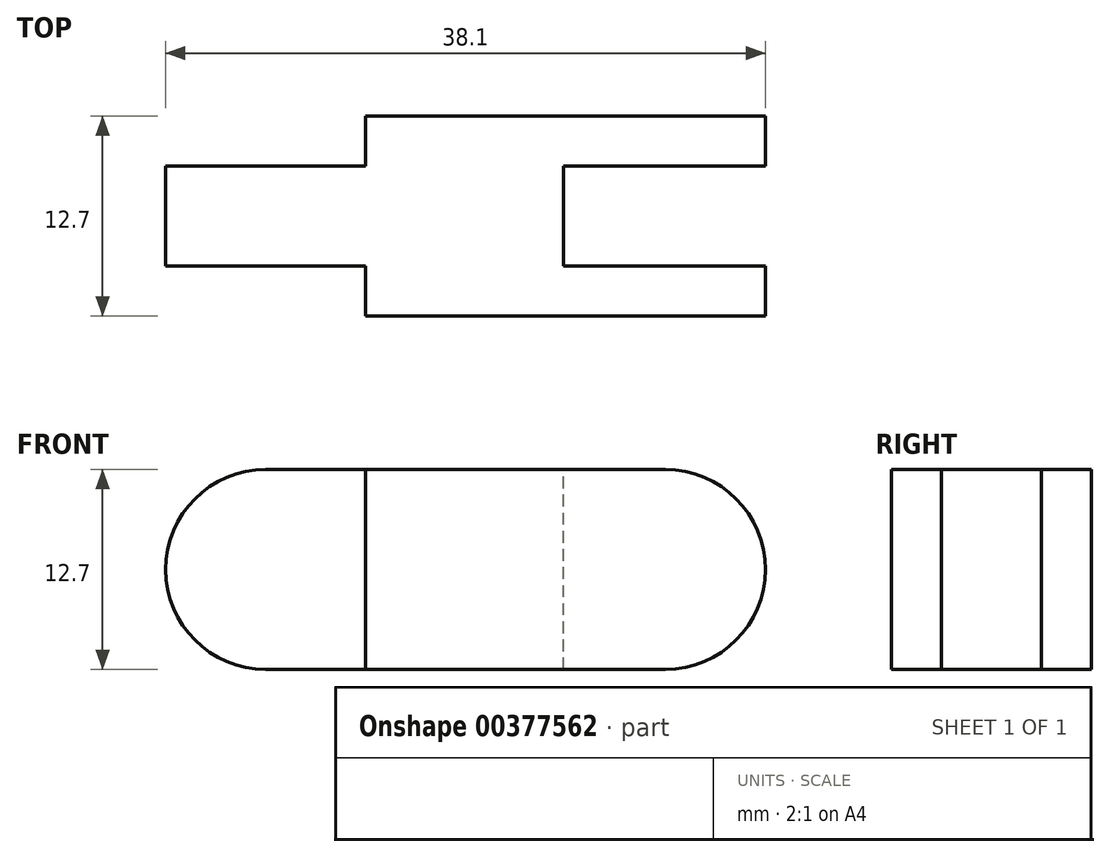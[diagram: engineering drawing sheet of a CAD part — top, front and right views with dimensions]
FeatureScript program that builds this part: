
annotation { "Feature Type Name" : "Feature", "Feature Type Description" : "" }
export const myFeature = defineFeature(function(context is Context, id is Id, definition is map)
    precondition{}
    {
        {
            var Q0;
            Q0=qCreatedBy(makeId("Front.planeOp"),FACE);
            var sketch = newSketch(context, id + "F0", { "sketchPlane" : qUnion([Q0])});
            skLineSegment(sketch, "E0.bottom", {"start": v(6.35, 0) * mm, "end": v(38.1, 0) * mm});
            skLineSegment(sketch, "E0.top", {"start": v(6.35, 12.7) * mm, "end": v(38.1, 12.7) * mm});
            skLineSegment(sketch, "E0.left", {"start": v(0, 6.35) * mm, "end": v(0, 6.35) * mm});
            skLineSegment(sketch, "E0.right", {"start": v(38.1, 0) * mm, "end": v(38.1, 12.7) * mm});
            skPoint(sketch, "E1.visualSharp", {"position": v(0, 12.7) * mm});
            skArc(sketch, "E1.filletArc", {"start": v(6.35, 12.7) * mm, "mid": v(1.86, 10.84) * mm, "end": v(0, 6.35) * mm});
            skPoint(sketch, "E2.visualSharp", {"position": v(0, 0) * mm});
            skArc(sketch, "E2.filletArc", {"start": v(0, 6.35) * mm, "mid": v(1.86, 1.86) * mm, "end": v(6.35, 0) * mm});
            skSolve(sketch);
        }
        {
            var Q0;
            Q0=qSketchRegion(id+"F0",true);
            extrude(context, id + "F1", {"entities" : qUnion([Q0]), "depth" : 3.17 * mm});
        }
        {
            var Q0;
            Q0=makeQuery(id+"F1.opExtrude","CAP_FACE",FACE,{"disambiguationData":[OSD([sQuery(id+"F0.wireOp",EDGE,"E0.bottom"),sQuery(id+"F0.wireOp",EDGE,"E0.top"),sQuery(id+"F0.wireOp",EDGE,"E0.right"),sQuery(id+"F0.wireOp",EDGE,"E1.filletArc"),sQuery(id+"F0.wireOp",EDGE,"E2.filletArc")])],"isStart":false});
            var sketch = newSketch(context, id + "F2", { "sketchPlane" : qUnion([Q0])});
            skLineSegment(sketch, "E3.bottom", {"start": v(38.1, 12.7) * mm, "end": v(12.7, 12.7) * mm});
            skLineSegment(sketch, "E3.top", {"start": v(38.1, 0) * mm, "end": v(12.7, 0) * mm});
            skLineSegment(sketch, "E3.left", {"start": v(38.1, 12.7) * mm, "end": v(38.1, 0) * mm});
            skLineSegment(sketch, "E3.right", {"start": v(12.7, 12.7) * mm, "end": v(12.7, 0) * mm});
            skSolve(sketch);
        }
        {
            var Q0;
            Q0=qSketchRegion(id+"F2",true);
            extrude(context, id + "F3", {"entities" : qUnion([Q0]), "operationType" : NewBodyOperationType.ADD, "depth" : 3.17 * mm});
        }
        {
            var Q0;
            Q0=makeQuery(id+"F3.boolean.opBoolean","MERGE",EDGE,{"derivedFrom":[makeQuery(id+"F1.opExtrude","SWEPT_EDGE",EDGE,{"disambiguationData":[OSD([sQuery(id+"F0.wireOp",EDGE,"E0.top"),sQuery(id+"F0.wireOp",EDGE,"E0.right")])]}),makeQuery(id+"F3.opExtrude","SWEPT_EDGE",EDGE,{"disambiguationData":[OSD([sQuery(id+"F2.wireOp",EDGE,"E3.bottom"),sQuery(id+"F2.wireOp",EDGE,"E3.left")])]})]});
            var Q1;
            Q1=makeQuery(id+"F3.boolean.opBoolean","MERGE",EDGE,{"derivedFrom":[makeQuery(id+"F1.opExtrude","SWEPT_EDGE",EDGE,{"disambiguationData":[OSD([sQuery(id+"F0.wireOp",EDGE,"E0.bottom"),sQuery(id+"F0.wireOp",EDGE,"E0.right")])]}),makeQuery(id+"F3.opExtrude","SWEPT_EDGE",EDGE,{"disambiguationData":[OSD([sQuery(id+"F2.wireOp",EDGE,"E3.top"),sQuery(id+"F2.wireOp",EDGE,"E3.left")])]})]});
            fillet(context, id + "F4", {"entities" : qUnion([Q0, Q1]), "radius" : 6.35 * mm, "tangentPropagation" : true, "allowEdgeOverflow" : false});
        }
        {
            var Q0;
            Q0=makeQuery(id+"F3.boolean.opBoolean","MERGE",FACE,{"derivedFrom":[makeQuery(id+"F1.opExtrude","SWEPT_FACE",FACE,{"disambiguationData":[OSD([sQuery(id+"F0.wireOp",EDGE,"E0.top")])]}),makeQuery(id+"F3.opExtrude","SWEPT_FACE",FACE,{"disambiguationData":[OSD([sQuery(id+"F2.wireOp",EDGE,"E3.bottom")])]})]});
            var sketch = newSketch(context, id + "F5", { "sketchPlane" : qUnion([Q0])});
            skPoint(sketch, "E4.oppositeSnap0", {"position": v(31.75, -3.18) * mm});
            skLineSegment(sketch, "E4.bottom", {"start": v(25.27, 0) * mm, "end": v(38.23, 0) * mm});
            skLineSegment(sketch, "E4.top", {"start": v(25.27, -3.18) * mm, "end": v(38.23, -3.18) * mm});
            skLineSegment(sketch, "E4.left", {"start": v(25.27, 0) * mm, "end": v(25.27, -3.18) * mm});
            skLineSegment(sketch, "E4.right", {"start": v(38.23, 0) * mm, "end": v(38.23, -3.17) * mm});
            skSolve(sketch);
        }
        {
            var Q0;
            Q0=qSketchRegion(id+"F5",true);
            extrude(context, id + "F6", {"entities" : qUnion([Q0]), "operationType" : NewBodyOperationType.REMOVE, "oppositeDirection" : true, "depth" : 25.4 * mm});
        }
        {
            var Q0;
            Q0=makeQuery(id+"F1.opExtrude","SWEPT_BODY",BODY,{"disambiguationData":[OSD([sQuery(id+"F0.wireOp",EDGE,"E0.bottom"),sQuery(id+"F0.wireOp",EDGE,"E0.top"),sQuery(id+"F0.wireOp",EDGE,"E0.right"),sQuery(id+"F0.wireOp",EDGE,"E1.filletArc"),sQuery(id+"F0.wireOp",EDGE,"E2.filletArc")])]});
            var Q1;
            Q1=makeQuery(id+"F1.opExtrude","CAP_FACE",FACE,{"disambiguationData":[OSD([sQuery(id+"F0.wireOp",EDGE,"E0.bottom"),sQuery(id+"F0.wireOp",EDGE,"E0.top"),sQuery(id+"F0.wireOp",EDGE,"E0.right"),sQuery(id+"F0.wireOp",EDGE,"E1.filletArc"),sQuery(id+"F0.wireOp",EDGE,"E2.filletArc")])],"isStart":true});
            mirror(context, id + "F7", {"operationType" : NewBodyOperationType.ADD, "entities" : qUnion([Q0]), "mirrorPlane" : qUnion([Q1])});
        }
    });
